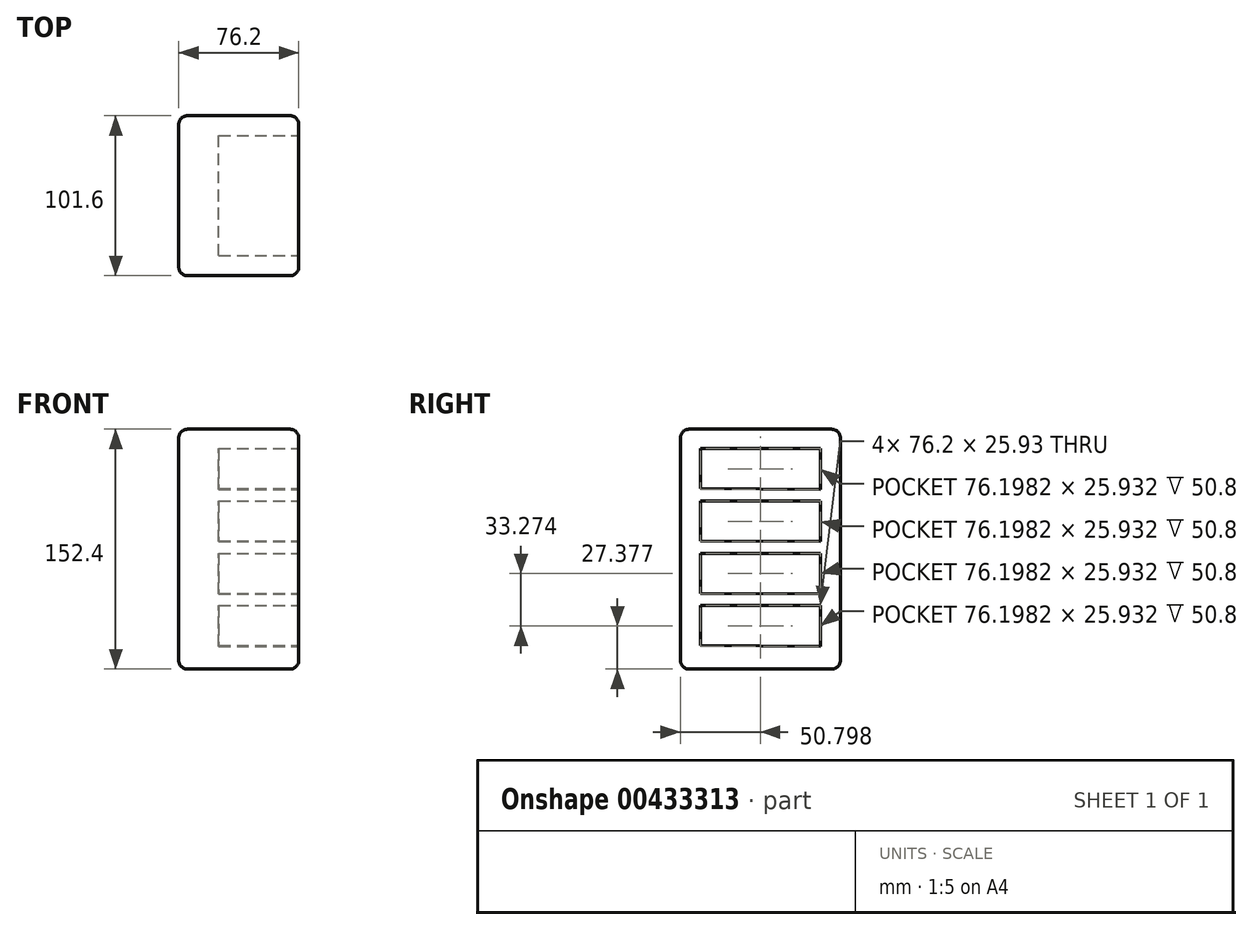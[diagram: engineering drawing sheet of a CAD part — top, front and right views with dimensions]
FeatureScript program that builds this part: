
annotation { "Feature Type Name" : "Feature", "Feature Type Description" : "" }
export const myFeature = defineFeature(function(context is Context, id is Id, definition is map)
    precondition{}
    {
        {
            var Q0;
            Q0=qCreatedBy(makeId("Top.planeOp"),FACE);
            var sketch = newSketch(context, id + "F0", { "sketchPlane" : qUnion([Q0])});
            skLineSegment(sketch, "E0.bottom", {"start": v(-43.35, 104.25) * mm, "end": v(32.85, 104.25) * mm});
            skLineSegment(sketch, "E0.top", {"start": v(-43.35, 2.65) * mm, "end": v(32.85, 2.65) * mm});
            skLineSegment(sketch, "E0.left", {"start": v(-43.35, 104.25) * mm, "end": v(-43.35, 2.65) * mm});
            skLineSegment(sketch, "E0.right", {"start": v(32.85, 104.25) * mm, "end": v(32.85, 2.65) * mm});
            skSolve(sketch);
        }
        {
            var Q0;
            Q0 = qSketchRegion(id + "F0", true);
            var Q1;
            Q1 = qSketchRegion(id + "FzJX93dI5asaO7x_1", true);
            extrude(context, id + "F1", {"entities" : qUnion([Q0, Q1]), "oppositeDirection" : true, "depth" : 152.4 * mm});
        }
        {
            var Q0;
            Q0=makeQuery(id+"F1.opExtrude","SWEPT_FACE",FACE,{"disambiguationData":[OSD([sQuery(id+"F0.wireOp",EDGE,"E0.right")])]});
            var sketch = newSketch(context, id + "F2", { "sketchPlane" : qUnion([Q0])});
            skLineSegment(sketch, "E1", {"start": v(91.55, -137.99) * mm, "end": v(91.55, -112.06) * mm});
            skLineSegment(sketch, "E2", {"start": v(91.55, -112.06) * mm, "end": v(15.35, -112.06) * mm});
            skLineSegment(sketch, "E3", {"start": v(15.35, -112.06) * mm, "end": v(15.35, -137.46) * mm});
            skLineSegment(sketch, "E4", {"start": v(15.35, -137.46) * mm, "end": v(91.55, -137.99) * mm});
            skLineSegment(sketch, "E5.0.1.0", {"start": v(15.35, -104.18) * mm, "end": v(91.55, -104.71) * mm});
            skLineSegment(sketch, "E5.0.1.1", {"start": v(91.55, -104.71) * mm, "end": v(91.55, -78.78) * mm});
            skLineSegment(sketch, "E5.0.1.2", {"start": v(91.55, -78.78) * mm, "end": v(15.35, -78.78) * mm});
            skLineSegment(sketch, "E5.0.1.3", {"start": v(15.35, -78.78) * mm, "end": v(15.35, -104.18) * mm});
            skLineSegment(sketch, "E5.0.2.0", {"start": v(15.35, -70.9) * mm, "end": v(91.55, -71.44) * mm});
            skLineSegment(sketch, "E5.0.2.1", {"start": v(91.55, -71.44) * mm, "end": v(91.55, -45.5) * mm});
            skLineSegment(sketch, "E5.0.2.2", {"start": v(91.55, -45.5) * mm, "end": v(15.35, -45.5) * mm});
            skLineSegment(sketch, "E5.0.2.3", {"start": v(15.35, -45.5) * mm, "end": v(15.35, -70.9) * mm});
            skLineSegment(sketch, "E5.0.3.0", {"start": v(15.35, -37.63) * mm, "end": v(91.55, -38.17) * mm});
            skLineSegment(sketch, "E5.0.3.1", {"start": v(91.55, -38.17) * mm, "end": v(91.55, -12.23) * mm});
            skLineSegment(sketch, "E5.0.3.2", {"start": v(91.55, -12.23) * mm, "end": v(15.35, -12.23) * mm});
            skLineSegment(sketch, "E5.0.3.3", {"start": v(15.35, -12.23) * mm, "end": v(15.35, -37.63) * mm});
            skLineSegment(sketch, "E5.direction1", {"start": v(15.35, -137.46) * mm, "end": v(15.35, -137.46) * mm});
            skLineSegment(sketch, "E5.direction2", {"start": v(15.35, -137.46) * mm, "end": v(15.35, -104.18) * mm, "construction": true});
            skSolve(sketch);
        }
        {
            var Q0;
            Q0=makeQuery(id+"F2.imprint","IMPRINT",FACE,{"disambiguationData":[TD([[makeQuery(id+"F2.imprint","IMPRINT",EDGE,{"derivedFrom":sQuery(id+"F2.wireOp",EDGE,"E1")}),1.0]])]});
            var Q1;
            Q1=makeQuery(id+"F2.imprint","IMPRINT",FACE,{"disambiguationData":[TD([[makeQuery(id+"F2.imprint","IMPRINT",EDGE,{"derivedFrom":sQuery(id+"F2.wireOp",EDGE,"E5.0.1.0")}),1.0]])]});
            var Q2;
            Q2=makeQuery(id+"F2.imprint","IMPRINT",FACE,{"disambiguationData":[TD([[makeQuery(id+"F2.imprint","IMPRINT",EDGE,{"derivedFrom":sQuery(id+"F2.wireOp",EDGE,"E5.0.2.0")}),1.0]])]});
            var Q3;
            Q3=makeQuery(id+"F2.imprint","IMPRINT",FACE,{"disambiguationData":[TD([[makeQuery(id+"F2.imprint","IMPRINT",EDGE,{"derivedFrom":sQuery(id+"F2.wireOp",EDGE,"E5.0.3.0")}),1.0]])]});
            extrude(context, id + "F3", {"entities" : qUnion([Q0, Q1, Q2, Q3]), "operationType" : NewBodyOperationType.REMOVE, "oppositeDirection" : true, "depth" : 50.8 * mm});
        }
        {
            var Q0;
            Q0=makeQuery(id+"F1.opExtrude","CAP_EDGE",EDGE,{"disambiguationData":[OSD([sQuery(id+"F0.wireOp",EDGE,"E0.bottom")])],"isStart":true});
            var Q1;
            Q1=makeQuery(id+"F1.opExtrude","CAP_EDGE",EDGE,{"disambiguationData":[OSD([sQuery(id+"F0.wireOp",EDGE,"E0.top")])],"isStart":true});
            var Q2;
            Q2=makeQuery(id+"F1.opExtrude","CAP_EDGE",EDGE,{"disambiguationData":[OSD([sQuery(id+"F0.wireOp",EDGE,"E0.top")])],"isStart":false});
            var Q3;
            Q3=makeQuery(id+"F1.opExtrude","CAP_EDGE",EDGE,{"disambiguationData":[OSD([sQuery(id+"F0.wireOp",EDGE,"E0.bottom")])],"isStart":false});
            var Q4;
            Q4=makeQuery(id+"F1.opExtrude","SWEPT_EDGE",EDGE,{"disambiguationData":[OSD([sQuery(id+"F0.wireOp",EDGE,"E0.top"),sQuery(id+"F0.wireOp",EDGE,"E0.right")])]});
            var Q5;
            Q5=makeQuery(id+"F1.opExtrude","CAP_EDGE",EDGE,{"disambiguationData":[OSD([sQuery(id+"F0.wireOp",EDGE,"E0.right")])],"isStart":false});
            var Q6;
            Q6=makeQuery(id+"F1.opExtrude","SWEPT_EDGE",EDGE,{"disambiguationData":[OSD([sQuery(id+"F0.wireOp",EDGE,"E0.bottom"),sQuery(id+"F0.wireOp",EDGE,"E0.right")])]});
            var Q7;
            Q7=makeQuery(id+"F1.opExtrude","CAP_EDGE",EDGE,{"disambiguationData":[OSD([sQuery(id+"F0.wireOp",EDGE,"E0.left")])],"isStart":false});
            var Q8;
            Q8=makeQuery(id+"F1.opExtrude","SWEPT_FACE",FACE,{"disambiguationData":[OSD([sQuery(id+"F0.wireOp",EDGE,"E0.top")])]});
            var Q9;
            Q9=makeQuery(id+"F1.opExtrude","CAP_EDGE",EDGE,{"disambiguationData":[OSD([sQuery(id+"F0.wireOp",EDGE,"E0.right")])],"isStart":true});
            var Q10;
            Q10=makeQuery(id+"F1.opExtrude","CAP_EDGE",EDGE,{"disambiguationData":[OSD([sQuery(id+"F0.wireOp",EDGE,"E0.left")])],"isStart":true});
            var Q11;
            Q11=makeQuery(id+"F1.opExtrude","SWEPT_FACE",FACE,{"disambiguationData":[OSD([sQuery(id+"F0.wireOp",EDGE,"E0.left")])]});
            fillet(context, id + "F4", {"entities" : qUnion([Q0, Q1, Q2, Q3, Q4, Q5, Q6, Q7, Q8, Q9, Q10, Q11]), "radius" : 5.52 * mm, "tangentPropagation" : true, "allowEdgeOverflow" : false});
        }
    });
